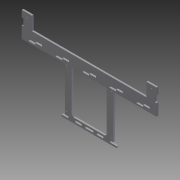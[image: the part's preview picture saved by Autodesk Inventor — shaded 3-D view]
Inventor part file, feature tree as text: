
AUTODESK INVENTOR PART (.ipt)
format: ipt  version: 2011 (Build 150239000, 239)  size: 592,896 bytes
history: native  units: in
note: dims shown in document units (in); Inventor stores cm internally (conversion verified against a paired STEP export)
features: extrude x21, sketch x21, fillet x2
ambient origin geometry x8: Origin, YZ Plane, XZ Plane, XY Plane, X Axis, Y Axis, Z Axis, Center Point
bodies: Solid1 (feature_tree)
feature tree (44):
  extrude  "Extrusion1"  Depth=41.5in
  extrude  "Extrusion2"  Depth=10.0in
  extrude  "Extrusion3"  Depth=0.6in
  extrude  "Extrusion4"  Depth=0.25in
  extrude  "Extrusion5"  Depth=0.5in
  extrude  "Extrusion6"  Depth=1.0in
  extrude  "Extrusion7"  Depth=4.1in TaperAngle=0.0deg
  extrude  "Extrusion8"  Depth=1.0in
  extrude  "Extrusion9"  Depth=1.0in
  extrude  "Extrusion10"  Depth=1.0in
  extrude  "Extrusion11"  Depth=4.1in TaperAngle=0.0deg
  extrude  "Extrusion12"  Depth=0.5in
  fillet  "Fillet1"  Radius=0.25in
  fillet  "Fillet2"  Radius=1.0in
  extrude  "Extrusion13"  Depth=3.0in
  extrude  "Extrusion14"  Depth=3.0in
  extrude  "Extrusion15"  Depth=3.0in
  extrude  "Extrusion16"  Depth=3.0in
  extrude  "Extrusion17"  Depth=3.0in
  extrude  "Extrusion18"  Depth=0.25in
  extrude  "Extrusion19"  Depth=0.25in TaperAngle=0.0deg
  extrude  "Extrusion20"  Depth=0.25in
  extrude  "Extrusion21"  Depth=1.0in
  sketch  "Sketch1"  dims[d0=20.0in d1=41.5in]
  sketch  "Sketch2"  dims[d2=0.25in d3=0.0in d4=10.0in]
  sketch  "Sketch3"  dims[d5=0.25in d6=0.6in]
  sketch  "Sketch4"  dims[d7=1.2in d8=0.25in]
  sketch  "Sketch5"  dims[d9=4.1in d10=0.0in d11=0.5in]
  sketch  "Sketch6"  dims[d12=0.5in d13=1.0in]
  sketch  "Sketch7"  dims[d14=1.0in d15=4.1in d16=0.0in]
  sketch  "Sketch8"  dims[d17=1.0in d18=1.0in]
  sketch  "Sketch9"  dims[d19=1.0in d20=1.0in]
  sketch  "Sketch10"  dims[d21=6.75in d22=1.0in]
  sketch  "Sketch11"  dims[d23=0.5in d24=4.1in d25=0.0in]
  sketch  "Sketch12"  dims[d26=0.25in d27=0.5in d28=0.25in d29=0.0in d30=1.0in]
  sketch  "Sketch13"  dims[d31=1.0in d32=3.0in]
  sketch  "Sketch14"  dims[d33=1.0in d34=3.0in]
  sketch  "Sketch15"  dims[d35=1.0in d36=3.0in]
  sketch  "Sketch16"  dims[d37=1.0in d38=3.0in]
  sketch  "Sketch17"  dims[d39=1.0in d40=3.0in]
  sketch  "Sketch18"  dims[d41=1.0in d42=0.25in]
  sketch  "Sketch19"  dims[d43=1.0in d44=0.0in d45=0.25in d46=0.0in]
  sketch  "Sketch20"  dims[d47=1.0in d48=0.25in]
  sketch  "Sketch21"  dims[d49=1.0in d50=1.0in d51=1.0in d52=1.0in d53=0.25in d54=0.0in d55=0.156in d56=0.156in d57=0.156in d58=0.156in d59=0.25in d60=0.0in d61=0.25in d62=0.0in d63=0.25in d64=0.0in d65=1.0in d66=1.0in d67=1.0in d68=1.0in d69=1.0in d70=1.0in d71=1.0in d72=1.0in d73=0.25in d74=0.0in d75=0.5in d76=0.5in d77=1.0in d78=0.0in d79=3.0in d80=3.0in d81=0.25in d82=0.0in d83=0.75in d84=0.75in d85=0.75in d86=0.75in d87=0.156in d88=0.156in d89=0.25in d90=0.0in d91=0.25in d92=1.0in d93=1.0in d94=1.0in d95=0.25in d96=0.0in d97=0.25in d98=1.0in d99=1.0in d100=1.0in d101=0.25in d102=0.0in d103=1.0in d104=0.0in d105=0.75in d106=0.5in d107=0.156in d108=0.156in d109=1.0in d110=0.0in d111=0.25in d112=0.0in d113=0.5in d114=0.5in d115=1.0in d116=0.25in d117=1.0in d118=1.0in d119=1.0in d120=1.0in d121=1.0in d122=1.0in d123=1.0in d124=1.0in d125=1.0in d126=1.0in d127=1.0in d128=1.0in d129=1.0in d130=1.0in d131=1.0in d132=1.0in d133=1.0in d134=1.0in d135=0.25in d136=0.0in]
